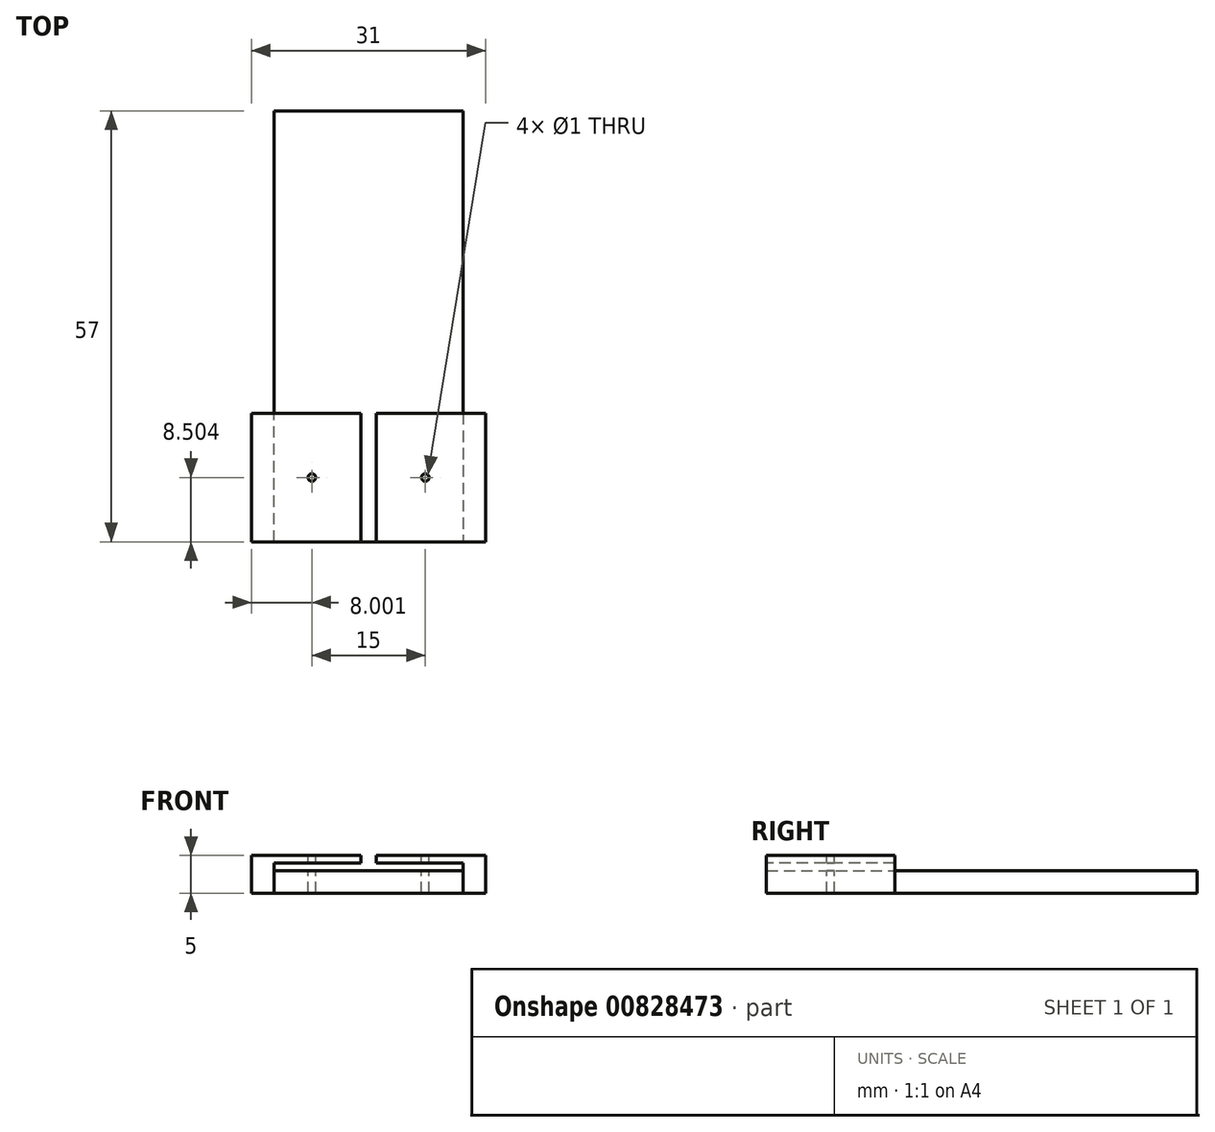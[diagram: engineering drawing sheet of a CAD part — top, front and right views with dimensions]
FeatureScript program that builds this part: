
annotation { "Feature Type Name" : "Feature", "Feature Type Description" : "" }
export const myFeature = defineFeature(function(context is Context, id is Id, definition is map)
    precondition{}
    {
        {
            var Q0;
            Q0=qCreatedBy(makeId("Top.planeOp"),FACE);
            var sketch = newSketch(context, id + "F0", { "sketchPlane" : qUnion([Q0])});
            skLineSegment(sketch, "E0.bottom", {"start": v(-36, -3.1) * mm, "end": v(44, -3.1) * mm});
            skLineSegment(sketch, "E0.top", {"start": v(-36, -20.1) * mm, "end": v(44, -20.1) * mm});
            skLineSegment(sketch, "E0.left", {"start": v(-36, -3.1) * mm, "end": v(-36, -20.1) * mm});
            skLineSegment(sketch, "E0.right", {"start": v(44, -3.1) * mm, "end": v(44, -20.1) * mm});
            skLineSegment(sketch, "E1", {"start": v(-4, -20.1) * mm, "end": v(-4, -3.1) * mm});
            skLineSegment(sketch, "E2", {"start": v(-4, -3.1) * mm, "end": v(-1, -3.1) * mm});
            skLineSegment(sketch, "E3", {"start": v(-1, -3.1) * mm, "end": v(-1, -20.1) * mm});
            skLineSegment(sketch, "E4", {"start": v(-1, -20.1) * mm, "end": v(-4, -20.1) * mm});
            skLineSegment(sketch, "E5", {"start": v(24, -20.1) * mm, "end": v(24, -3.1) * mm});
            skLineSegment(sketch, "E6", {"start": v(24, -3.1) * mm, "end": v(27, -3.1) * mm});
            skLineSegment(sketch, "E7", {"start": v(27, -3.1) * mm, "end": v(27, -20.1) * mm});
            skLineSegment(sketch, "E8", {"start": v(27, -20.1) * mm, "end": v(24, -20.1) * mm});
            skLineSegment(sketch, "E9", {"start": v(-1, -3.1) * mm, "end": v(-1, 36.9) * mm});
            skLineSegment(sketch, "E10", {"start": v(-1, 36.9) * mm, "end": v(-36, 36.9) * mm});
            skLineSegment(sketch, "E11", {"start": v(-36, 36.9) * mm, "end": v(-36, -3.1) * mm});
            skLineSegment(sketch, "E12", {"start": v(24, -3.1) * mm, "end": v(24, 36.9) * mm});
            skLineSegment(sketch, "E13", {"start": v(24, 36.9) * mm, "end": v(44, 36.9) * mm});
            skLineSegment(sketch, "E14", {"start": v(44, 36.9) * mm, "end": v(44, -3.1) * mm});
            skLineSegment(sketch, "E15", {"start": v(-1, 36.9) * mm, "end": v(24, 36.9) * mm});
            skSolve(sketch);
        }
        {
            var Q0;
            {var subQ0=sQuery(id+"F0.wireOp",EDGE,"E3");Q0=makeQuery(id+"F0.imprint","IMPRINT",FACE,{"disambiguationData":[TD([[makeQuery(id+"F0.imprint","IMPRINT",EDGE,{"derivedFrom":subQ0}),1.0]])]});}
            var Q1;
            {var subQ0=sQuery(id+"F0.wireOp",EDGE,"E2");Q1=makeQuery(id+"F0.imprint","IMPRINT",FACE,{"disambiguationData":[TD([[makeQuery(id+"F0.imprint","IMPRINT",EDGE,{"derivedFrom":subQ0}),1.0]])]});}
            var Q2;
            {var subQ0=sQuery(id+"F0.wireOp",EDGE,"E9");Q2=makeQuery(id+"F0.imprint","IMPRINT",FACE,{"disambiguationData":[TD([[makeQuery(id+"F0.imprint","IMPRINT",EDGE,{"derivedFrom":subQ0}),-1.0]])]});}
            var Q3;
            {var subQ0=sQuery(id+"F0.wireOp",EDGE,"E6");Q3=makeQuery(id+"F0.imprint","IMPRINT",FACE,{"disambiguationData":[TD([[makeQuery(id+"F0.imprint","IMPRINT",EDGE,{"derivedFrom":subQ0}),1.0]])]});}
            extrude(context, id + "F1", {"entities" : qUnion([Q0, Q1, Q2, Q3]), "depth" : 3 * mm, "offsetDistance" : 25.4 * mm});
        }
        {
            var Q0;
            Q0=makeQuery(id+"F0.imprint","IMPRINT",FACE,{"disambiguationData":[TD([[makeQuery(id+"F0.imprint","IMPRINT",EDGE,{"derivedFrom":sQuery(id+"F0.wireOp",EDGE,"E1")}),-1.0]])]});
            var Q1;
            Q1=makeQuery(id+"F0.imprint","IMPRINT",FACE,{"disambiguationData":[TD([[makeQuery(id+"F0.imprint","IMPRINT",EDGE,{"derivedFrom":sQuery(id+"F0.wireOp",EDGE,"E5")}),-1.0]])]});
            extrude(context, id + "F2", {"entities" : qUnion([Q0, Q1]), "depth" : 5 * mm, "offsetDistance" : 25.4 * mm});
        }
        {
            var Q0;
            Q0=makeQuery(id+"F2.opExtrude","SWEPT_FACE",FACE,{"disambiguationData":[OSD([sQuery(id+"F0.wireOp",EDGE,"E3")])]});
            var sketch = newSketch(context, id + "F3", { "sketchPlane" : qUnion([Q0])});
            skLineSegment(sketch, "E16", {"start": v(-20.1, 5) * mm, "end": v(-20.1, 4) * mm});
            skLineSegment(sketch, "E17", {"start": v(-20.1, 4) * mm, "end": v(-3.1, 4) * mm});
            skLineSegment(sketch, "E18", {"start": v(-3.1, 4) * mm, "end": v(-3.1, 5) * mm});
            skLineSegment(sketch, "E19", {"start": v(-3.1, 5) * mm, "end": v(-20.1, 5) * mm});
            skSolve(sketch);
        }
        {
            var Q0;
            Q0=makeQuery(id+"F3.imprint","IMPRINT",FACE,{"disambiguationData":[TD([[makeQuery(id+"F3.imprint","IMPRINT",EDGE,{"derivedFrom":sQuery(id+"F3.wireOp",EDGE,"E16")}),1.0]])]});
            extrude(context, id + "F4", {"entities" : qUnion([Q0]), "operationType" : NewBodyOperationType.ADD, "depth" : 11.5 * mm, "offsetDistance" : 25.4 * mm});
        }
        {
            var Q0;
            Q0=makeQuery(id+"F2.opExtrude","SWEPT_FACE",FACE,{"disambiguationData":[OSD([sQuery(id+"F0.wireOp",EDGE,"E5")])]});
            var sketch = newSketch(context, id + "F5", { "sketchPlane" : qUnion([Q0])});
            skLineSegment(sketch, "E20", {"start": v(3.1, 5) * mm, "end": v(3.1, 4) * mm});
            skLineSegment(sketch, "E21", {"start": v(3.1, 4) * mm, "end": v(20.1, 4) * mm});
            skLineSegment(sketch, "E22", {"start": v(20.1, 4) * mm, "end": v(20.1, 5) * mm});
            skLineSegment(sketch, "E23", {"start": v(20.1, 5) * mm, "end": v(3.1, 5) * mm});
            skSolve(sketch);
        }
        {
            var Q0;
            Q0=makeQuery(id+"F5.imprint","IMPRINT",FACE,{"disambiguationData":[TD([[makeQuery(id+"F5.imprint","IMPRINT",EDGE,{"derivedFrom":sQuery(id+"F5.wireOp",EDGE,"E20")}),1.0]])]});
            extrude(context, id + "F6", {"entities" : qUnion([Q0]), "operationType" : NewBodyOperationType.ADD, "depth" : 11.5 * mm, "offsetDistance" : 25.4 * mm});
        }
        {
            var Q0;
            Q0=makeQuery(id+"F4.boolean.opBoolean","MERGE",FACE,{"derivedFrom":[makeQuery(id+"F2.opExtrude","CAP_FACE",FACE,{"disambiguationData":[OSD([sQuery(id+"F0.wireOp",EDGE,"E1"),sQuery(id+"F0.wireOp",EDGE,"E2"),sQuery(id+"F0.wireOp",EDGE,"E3"),sQuery(id+"F0.wireOp",EDGE,"E4")])],"isStart":false}),makeQuery(id+"F4.opExtrude","SWEPT_FACE",FACE,{"disambiguationData":[OSD([sQuery(id+"F3.wireOp",EDGE,"E19")])]})]});
            var sketch = newSketch(context, id + "F7", { "sketchPlane" : qUnion([Q0])});
            skCircle(sketch, "E24", {"center": v(4, -11.6) * mm, "radius": 1.5 * mm});
            skLineSegment(sketch, "E25", {"start": v(4, -11.6) * mm, "end": v(-4, -11.6) * mm});
            skLineSegment(sketch, "E26", {"start": v(-4, -11.6) * mm, "end": v(-4, -3.1) * mm});
            skLineSegment(sketch, "E27", {"start": v(-4, -3.1) * mm, "end": v(4, -3.1) * mm});
            skLineSegment(sketch, "E28", {"start": v(4, -3.1) * mm, "end": v(4, -11.6) * mm});
            skSolve(sketch);
        }
        {
            var Q0;
            Q0=sQuery(id+"F7.wireOp",VERTEX,"E25.start");
            var Q1;
            Q1=makeQuery(id+"F2.opExtrude","SWEPT_BODY",BODY,{"disambiguationData":[OSD([sQuery(id+"F0.wireOp",EDGE,"E1"),sQuery(id+"F0.wireOp",EDGE,"E2"),sQuery(id+"F0.wireOp",EDGE,"E3"),sQuery(id+"F0.wireOp",EDGE,"E4")])]});
            var Q2;
            Q2=makeQuery(id+"F1.opExtrude","SWEPT_BODY",BODY,{"disambiguationData":[OSD([sQuery(id+"F0.wireOp",EDGE,"E0.bottom"),sQuery(id+"F0.wireOp",EDGE,"E0.top"),sQuery(id+"F0.wireOp",EDGE,"E2"),sQuery(id+"F0.wireOp",EDGE,"E3"),sQuery(id+"F0.wireOp",EDGE,"E5"),sQuery(id+"F0.wireOp",EDGE,"E6"),sQuery(id+"F0.wireOp",EDGE,"E10"),sQuery(id+"F0.wireOp",EDGE,"E11"),sQuery(id+"F0.wireOp",EDGE,"E13"),sQuery(id+"F0.wireOp",EDGE,"E14"),sQuery(id+"F0.wireOp",EDGE,"E15")])]});
            hole(context, id + "F8", {"style" : HoleStyle.SIMPLE, "endStyle" : HoleEndStyle.THROUGH, "holeDiameter" : 1 * mm, "majorDiameter" : 6.35 * mm, "isTappedThrough" : true, "tappedDepth" : 12.7 * mm, "tapClearance" : 3, "locations" : qUnion([Q0]), "scope" : qUnion([Q1, Q2])});
        }
        {
            var Q0;
            Q0=makeQuery(id+"F6.boolean.opBoolean","MERGE",FACE,{"derivedFrom":[makeQuery(id+"F2.opExtrude","CAP_FACE",FACE,{"disambiguationData":[OSD([sQuery(id+"F0.wireOp",EDGE,"E5"),sQuery(id+"F0.wireOp",EDGE,"E6"),sQuery(id+"F0.wireOp",EDGE,"E7"),sQuery(id+"F0.wireOp",EDGE,"E8")])],"isStart":false}),makeQuery(id+"F6.opExtrude","SWEPT_FACE",FACE,{"disambiguationData":[OSD([sQuery(id+"F5.wireOp",EDGE,"E23")])]})]});
            var sketch = newSketch(context, id + "F9", { "sketchPlane" : qUnion([Q0])});
            skCircle(sketch, "E29", {"center": v(19, -11.6) * mm, "radius": 1.5 * mm});
            skLineSegment(sketch, "E30", {"start": v(19, -11.6) * mm, "end": v(19, -3.1) * mm});
            skLineSegment(sketch, "E31", {"start": v(19, -11.6) * mm, "end": v(27, -11.6) * mm});
            skSolve(sketch);
        }
        {
            var Q0;
            Q0=sQuery(id+"F9.wireOp",VERTEX,"E30.start");
            var Q1;
            Q1=makeQuery(id+"F2.opExtrude","SWEPT_BODY",BODY,{"disambiguationData":[OSD([sQuery(id+"F0.wireOp",EDGE,"E5"),sQuery(id+"F0.wireOp",EDGE,"E6"),sQuery(id+"F0.wireOp",EDGE,"E7"),sQuery(id+"F0.wireOp",EDGE,"E8")])]});
            var Q2;
            Q2=makeQuery(id+"F1.opExtrude","SWEPT_BODY",BODY,{"disambiguationData":[OSD([sQuery(id+"F0.wireOp",EDGE,"E0.bottom"),sQuery(id+"F0.wireOp",EDGE,"E0.top"),sQuery(id+"F0.wireOp",EDGE,"E2"),sQuery(id+"F0.wireOp",EDGE,"E3"),sQuery(id+"F0.wireOp",EDGE,"E5"),sQuery(id+"F0.wireOp",EDGE,"E6"),sQuery(id+"F0.wireOp",EDGE,"E10"),sQuery(id+"F0.wireOp",EDGE,"E11"),sQuery(id+"F0.wireOp",EDGE,"E13"),sQuery(id+"F0.wireOp",EDGE,"E14"),sQuery(id+"F0.wireOp",EDGE,"E15")])]});
            hole(context, id + "F10", {"style" : HoleStyle.SIMPLE, "endStyle" : HoleEndStyle.THROUGH, "holeDiameter" : 1 * mm, "majorDiameter" : 6.35 * mm, "isTappedThrough" : true, "tappedDepth" : 12.7 * mm, "tapClearance" : 3, "locations" : qUnion([Q0]), "scope" : qUnion([Q1, Q2])});
        }
    });
